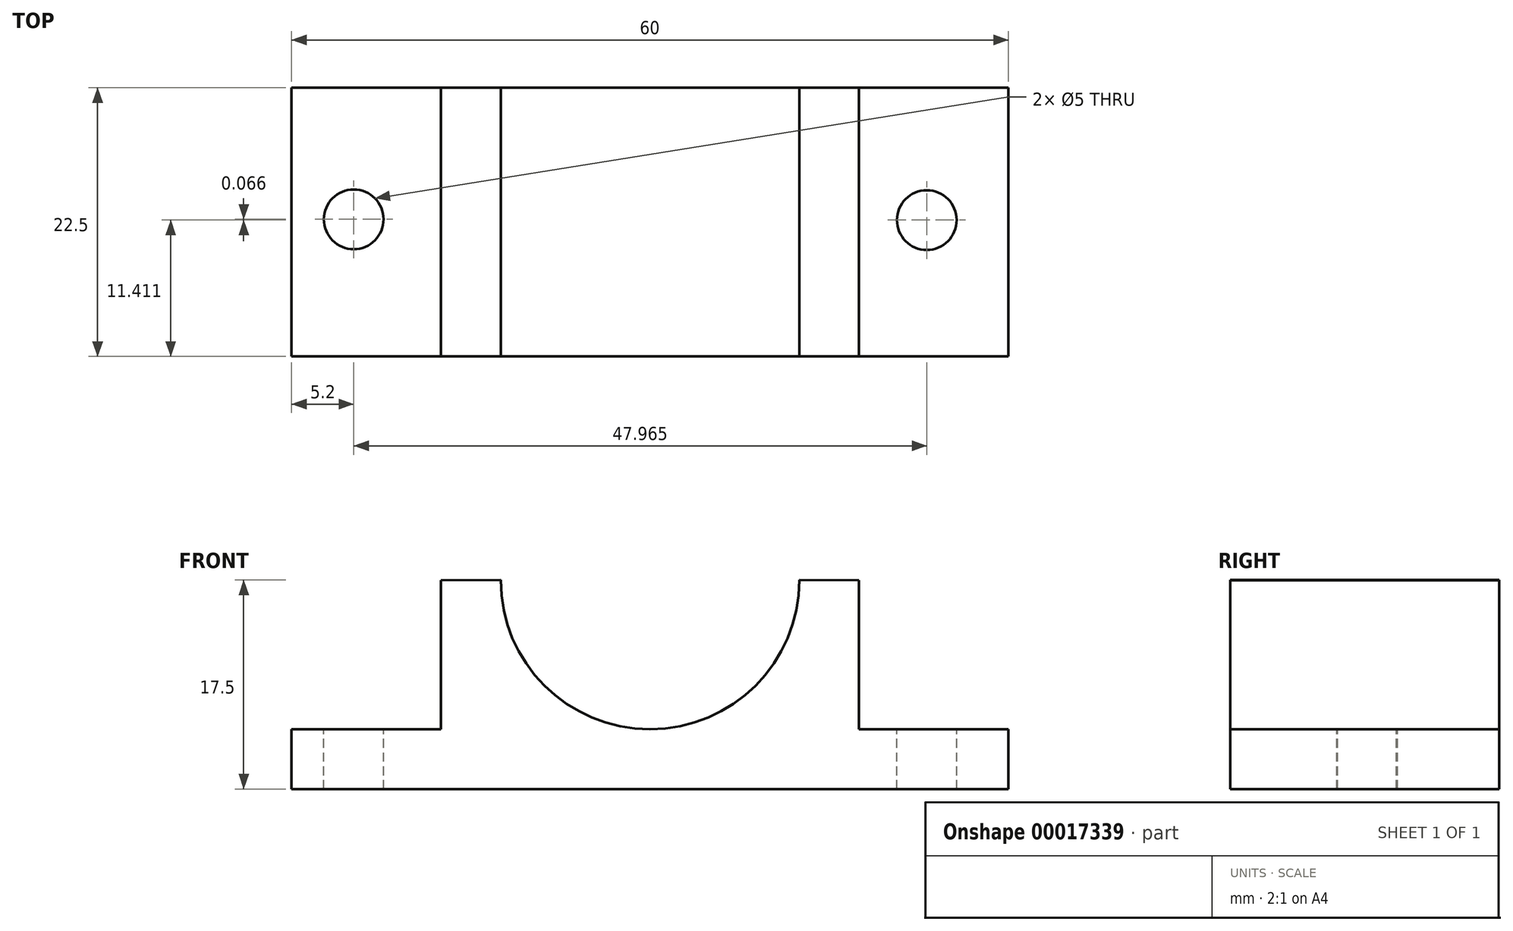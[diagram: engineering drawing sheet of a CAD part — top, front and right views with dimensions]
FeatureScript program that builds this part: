
annotation { "Feature Type Name" : "Feature", "Feature Type Description" : "" }
export const myFeature = defineFeature(function(context is Context, id is Id, definition is map)
    precondition{}
    {
        {
            var Q0;
            Q0=qCreatedBy(makeId("Front.planeOp"),FACE);
            var sketch = newSketch(context, id + "F0", { "sketchPlane" : qUnion([Q0])});
            skLineSegment(sketch, "E0", {"start": v(-17.5, -6.13) * mm, "end": v(-17.5, -1.13) * mm});
            skLineSegment(sketch, "E1", {"start": v(-17.5, -1.13) * mm, "end": v(-5, -1.13) * mm});
            skLineSegment(sketch, "E2", {"start": v(-5, -1.13) * mm, "end": v(-5, 11.37) * mm});
            skLineSegment(sketch, "E3", {"start": v(30, 11.37) * mm, "end": v(30, -1.13) * mm});
            skLineSegment(sketch, "E4", {"start": v(30, -1.13) * mm, "end": v(42.5, -1.13) * mm});
            skLineSegment(sketch, "E5", {"start": v(42.5, -1.13) * mm, "end": v(42.5, -6.13) * mm});
            skLineSegment(sketch, "E6", {"start": v(42.5, -6.13) * mm, "end": v(-17.5, -6.13) * mm});
            skArc(sketch, "E7", {"start": v(0, 11.37) * mm, "mid": v(12.5, -1.13) * mm, "end": v(25, 11.37) * mm});
            skLineSegment(sketch, "E8", {"start": v(-5, 11.37) * mm, "end": v(0, 11.37) * mm});
            skLineSegment(sketch, "E9", {"start": v(25, 11.37) * mm, "end": v(30, 11.37) * mm});
            skSolve(sketch);
        }
        {
            var Q0;
            Q0=makeQuery(id+"F0.imprint","IMPRINT",FACE,{"disambiguationData":[TD([[makeQuery(id+"F0.imprint","IMPRINT",EDGE,{"derivedFrom":sQuery(id+"F0.wireOp",EDGE,"E0")}),-1.0]])]});
            extrude(context, id + "F1", {"entities" : qUnion([Q0]), "oppositeDirection" : true, "depth" : 22.5 * mm});
        }
        {
            var Q0;
            Q0=makeQuery(id+"F1.opExtrude","SWEPT_FACE",FACE,{"disambiguationData":[OSD([sQuery(id+"F0.wireOp",EDGE,"E1")])]});
            var sketch = newSketch(context, id + "F2", { "sketchPlane" : qUnion([Q0])});
            skCircle(sketch, "E10", {"center": v(-12.3, 11.48) * mm, "radius": 2.5 * mm});
            skSolve(sketch);
        }
        {
            var Q0;
            Q0=makeQuery(id+"F2.imprint","IMPRINT",FACE,{"disambiguationData":[TD([[makeQuery(id+"F2.imprint","IMPRINT",EDGE,{"derivedFrom":sQuery(id+"F2.wireOp",EDGE,"E10")}),1.0]])]});
            extrude(context, id + "F3", {"entities" : qUnion([Q0]), "operationType" : NewBodyOperationType.REMOVE, "oppositeDirection" : true, "depth" : 25 * mm});
        }
        {
            var Q0;
            Q0=makeQuery(id+"F1.opExtrude","SWEPT_FACE",FACE,{"disambiguationData":[OSD([sQuery(id+"F0.wireOp",EDGE,"E4")])]});
            var sketch = newSketch(context, id + "F4", { "sketchPlane" : qUnion([Q0])});
            skCircle(sketch, "E11", {"center": v(35.66, 11.41) * mm, "radius": 2.5 * mm});
            skSolve(sketch);
        }
        {
            var Q0;
            Q0=makeQuery(id+"F4.imprint","IMPRINT",FACE,{"disambiguationData":[TD([[makeQuery(id+"F4.imprint","IMPRINT",EDGE,{"derivedFrom":sQuery(id+"F4.wireOp",EDGE,"E11")}),1.0]])]});
            extrude(context, id + "F5", {"entities" : qUnion([Q0]), "operationType" : NewBodyOperationType.REMOVE, "oppositeDirection" : true, "depth" : 25 * mm});
        }
    });
